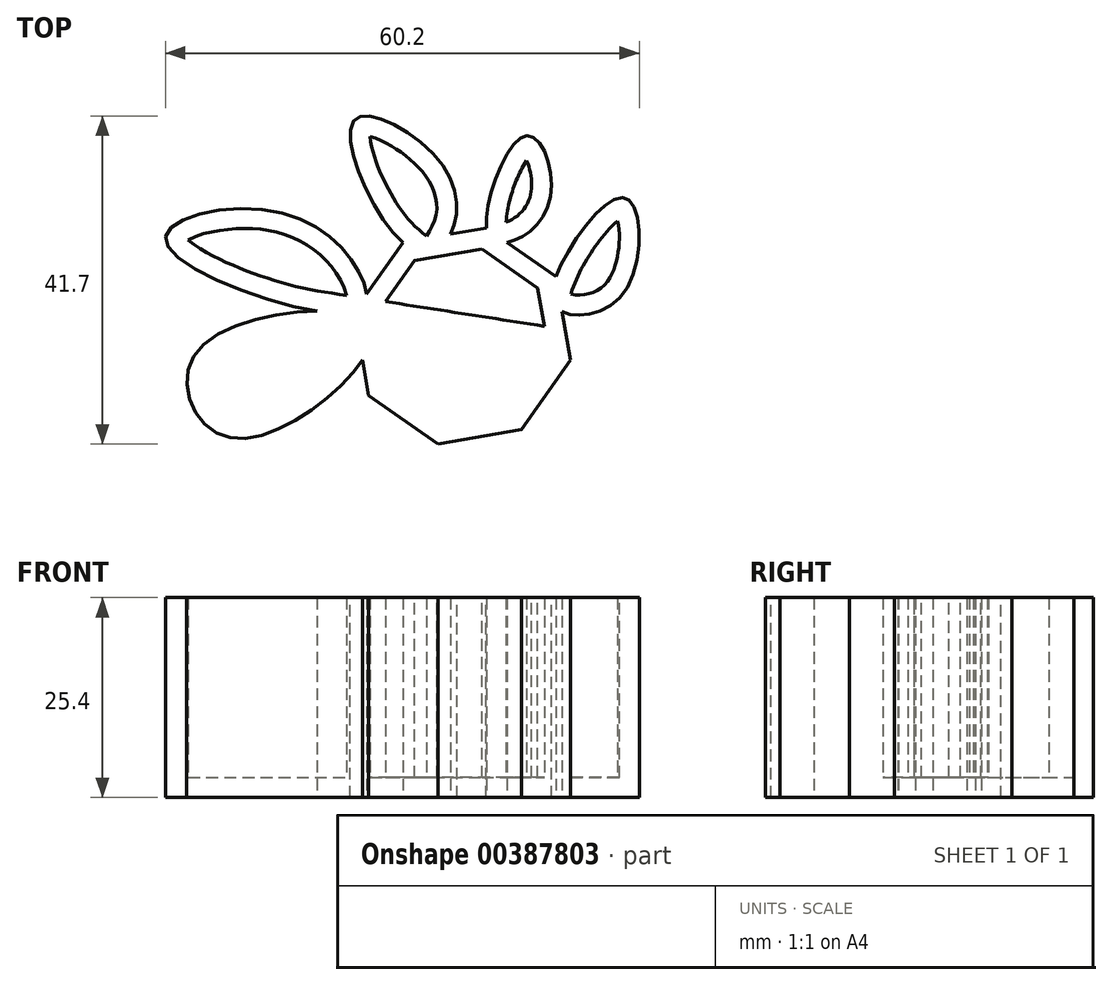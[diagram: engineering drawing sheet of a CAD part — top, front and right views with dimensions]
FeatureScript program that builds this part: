
annotation { "Feature Type Name" : "Feature", "Feature Type Description" : "" }
export const myFeature = defineFeature(function(context is Context, id is Id, definition is map)
    precondition{}
    {
        {
            var Q0;
            Q0=qCreatedBy(makeId("Top.planeOp"),FACE);
            var sketch = newSketch(context, id + "F0", { "sketchPlane" : qUnion([Q0])});
            skArc(sketch, "E0.cCircle", {"start": v(-12.65, -3.05) * mm, "mid": v(3.07, -12.64) * mm, "end": v(12.64, 3.1) * mm, "construction": true});
            skLineSegment(sketch, "E0.0", {"start": v(13.74, -3.08) * mm, "end": v(7.54, -11.9) * mm});
            skLineSegment(sketch, "E0.1", {"start": v(7.54, -11.9) * mm, "end": v(-3.08, -13.74) * mm});
            skLineSegment(sketch, "E0.2", {"start": v(-3.08, -13.74) * mm, "end": v(-11.9, -7.54) * mm});
            skLineSegment(sketch, "E0.3", {"start": v(-11.9, -7.54) * mm, "end": v(-12.67, -3.08) * mm});
            skLineSegment(sketch, "E0.4", {"start": v(-12.16, 5.33) * mm, "end": v(-7.54, 11.9) * mm});
            skLineSegment(sketch, "E0.5", {"start": v(-2.23, 12.82) * mm, "end": v(3.08, 13.74) * mm});
            skLineSegment(sketch, "E0.6", {"start": v(5.7, 11.9) * mm, "end": v(11.9, 7.54) * mm});
            skLineSegment(sketch, "E0.7", {"start": v(12.67, 3.08) * mm, "end": v(13.74, -3.08) * mm});
            skPoint(sketch, "E0.0.midPoint", {"position": v(10.64, -7.49) * mm});
            skPoint(sketch, "E1.3.internal.snap0", {"position": v(-10.64, 7.49) * mm});
            skPoint(sketch, "E1.3.internal.snap1", {"position": v(-12.82, -2.23) * mm});
            skFitSpline(sketch, "E1", {"points": [v(-13.74, 3.08) * mm, v(-37.64, 11.9) * mm, v(-24.44, 15.96) * mm, v(-12.82, 7.49) * mm, v(-13.74, 3.08) * mm]});
            skPoint(sketch, "E2.2.internal.snap0", {"position": v(-2.23, 12.82) * mm});
            skPoint(sketch, "E2.3.internal.snap0", {"position": v(-2.23, 12.82) * mm});
            skFitSpline(sketch, "E2", {"points": [v(-7.54, 11.9) * mm, v(-13.74, 27.4) * mm, v(-2.23, 21.28) * mm, v(-2.23, 11.9) * mm, v(-7.54, 11.9) * mm]});
            skFitSpline(sketch, "E3", {"points": [v(3.08, 13.74) * mm, v(8.08, 25.42) * mm, v(11.23, 17.74) * mm, v(5.7, 11.9) * mm, v(3.08, 13.74) * mm]});
            skFitSpline(sketch, "E4", {"points": [v(11.9, 7.54) * mm, v(20.7, 17.54) * mm, v(20.7, 5.72) * mm, v(12.67, 3.08) * mm, v(11.9, 7.54) * mm]});
            skFitSpline(sketch, "E5", {"points": [v(-12.67, -3.08) * mm, v(-29.95, -12.8) * mm, v(-33.9, -2.23) * mm, v(-12.82, 2.23) * mm, v(-12.67, -3.08) * mm]});
            skArc(sketch, "E6.trimOffspring", {"start": v(-6.59, 11.22) * mm, "mid": v(-10.12, 8.18) * mm, "end": v(-12.35, 4.08) * mm, "construction": true});
            skArc(sketch, "E7.trimOffspring", {"start": v(3.52, 12.53) * mm, "mid": v(0.66, 13) * mm, "end": v(-2.23, 12.82) * mm, "construction": true});
            skArc(sketch, "E8.trimOffspring", {"start": v(11.48, 6.12) * mm, "mid": v(8.9, 9.5) * mm, "end": v(5.38, 11.85) * mm, "construction": true});
            skSolve(sketch);
        }
        {
            var Q0;
            Q0 = qSketchRegion(id + "F0", true);
            extrude(context, id + "F1", {"entities" : qUnion([Q0]), "depth" : 25.4 * mm});
        }
        {
            var Q0;
            Q0=makeQuery(id+"F1.opExtrude","CAP_FACE",FACE,{"disambiguationData":[OSD([sQuery(id+"F0.wireOp",EDGE,"E0.0"),sQuery(id+"F0.wireOp",EDGE,"E0.1"),sQuery(id+"F0.wireOp",EDGE,"E0.2"),sQuery(id+"F0.wireOp",EDGE,"E0.3"),sQuery(id+"F0.wireOp",EDGE,"E0.4"),sQuery(id+"F0.wireOp",EDGE,"E0.5"),sQuery(id+"F0.wireOp",EDGE,"E0.6"),sQuery(id+"F0.wireOp",EDGE,"E0.7"),sQuery(id+"F0.wireOp",EDGE,"E1"),sQuery(id+"F0.wireOp",EDGE,"E2"),sQuery(id+"F0.wireOp",EDGE,"E3"),sQuery(id+"F0.wireOp",EDGE,"E4"),sQuery(id+"F0.wireOp",EDGE,"E5")])],"isStart":false});
            shell(context, id + "F2", {"entities" : qUnion([Q0]), "thickness" : 2.54 * mm});
        }
    });
